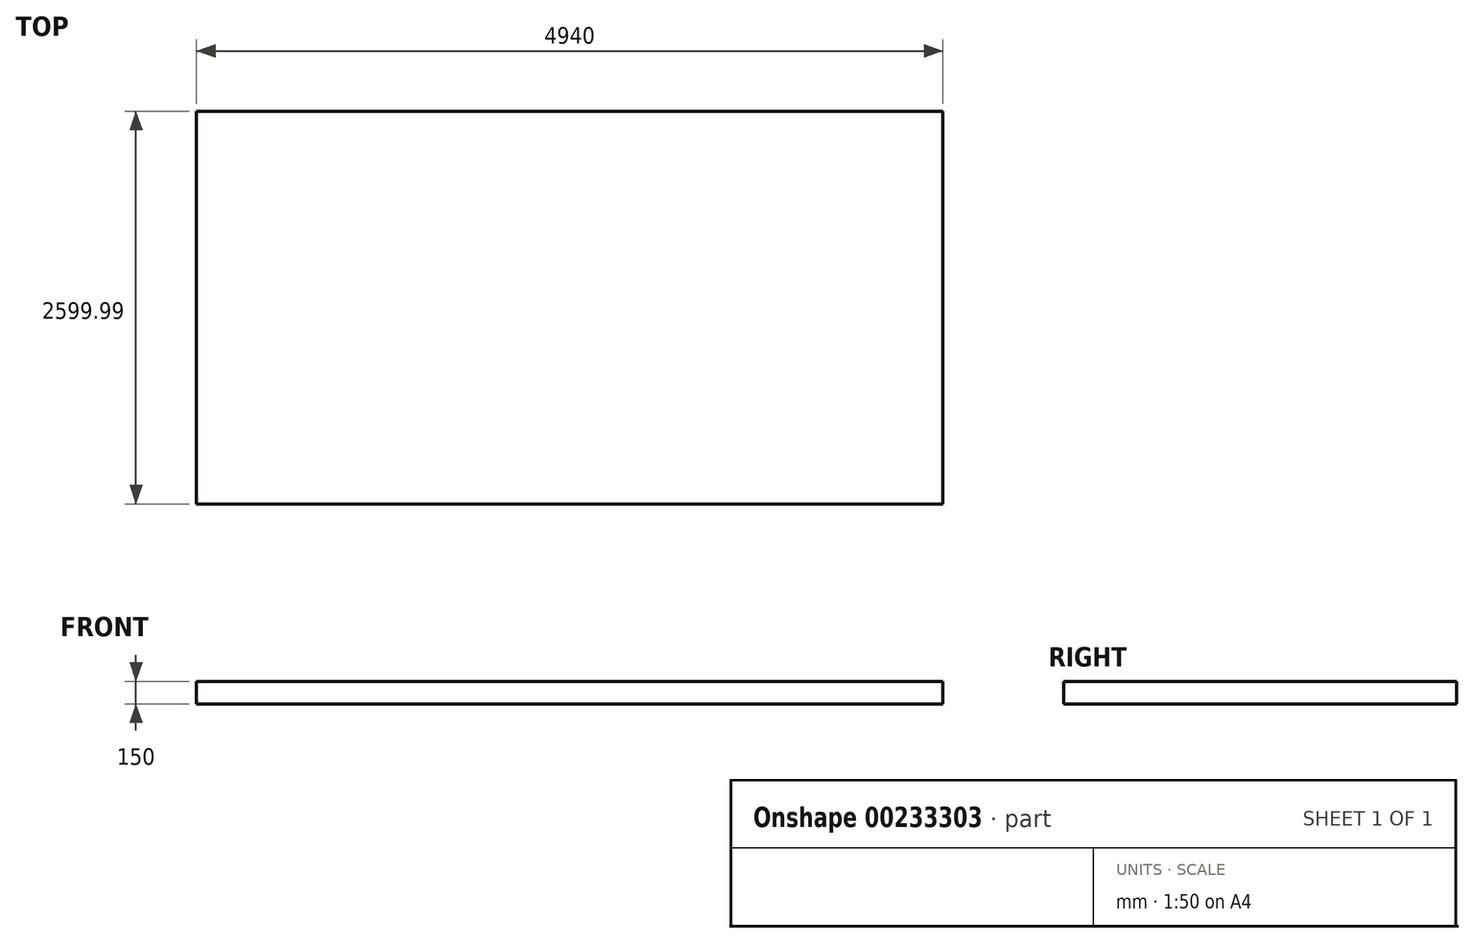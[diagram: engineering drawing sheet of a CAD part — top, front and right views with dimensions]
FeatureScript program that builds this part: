
annotation { "Feature Type Name" : "Feature", "Feature Type Description" : "" }
export const myFeature = defineFeature(function(context is Context, id is Id, definition is map)
    precondition{}
    {
        {
            var Q0;
            Q0=qCreatedBy(makeId("Front.planeOp"),FACE);
            var sketch = newSketch(context, id + "F0", { "sketchPlane" : qUnion([Q0])});
            skLineSegment(sketch, "E0", {"start": v(-2513.03, 784.82) * mm, "end": v(-2513.03, 634.82) * mm});
            skLineSegment(sketch, "E1", {"start": v(-2513.03, 634.82) * mm, "end": v(2426.97, 634.82) * mm});
            skLineSegment(sketch, "E2", {"start": v(2426.97, 634.82) * mm, "end": v(2426.97, 784.82) * mm});
            skLineSegment(sketch, "E3", {"start": v(2426.97, 784.82) * mm, "end": v(-2513.03, 784.82) * mm});
            skSolve(sketch);
        }
        {
            var Q0;
            Q0 = qSketchRegion(id + "F0", true);
            extrude(context, id + "F1", {"entities" : qUnion([Q0]), "depth" : 2600 * mm});
        }
    });
